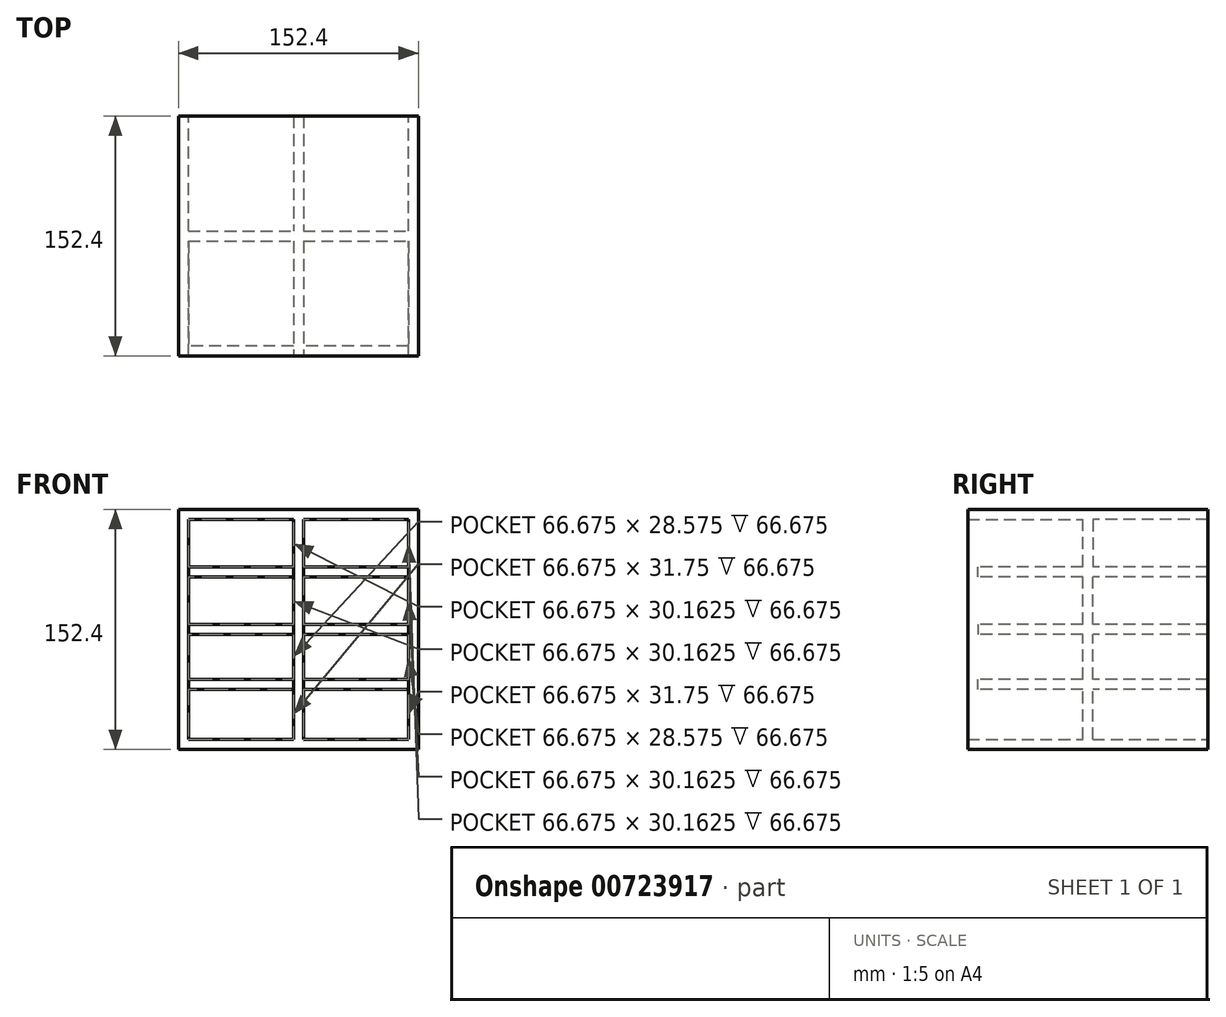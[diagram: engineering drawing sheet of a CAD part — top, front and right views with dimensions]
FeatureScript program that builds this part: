
annotation { "Feature Type Name" : "Feature", "Feature Type Description" : "" }
export const myFeature = defineFeature(function(context is Context, id is Id, definition is map)
    precondition{}
    {
        {
            var Q0;
            Q0=qCreatedBy(makeId("Front.planeOp"),FACE);
            var sketch = newSketch(context, id + "F0", { "sketchPlane" : qUnion([Q0])});
            skLineSegment(sketch, "E0.bottom", {"start": v(76.2, 76.2) * mm, "end": v(-76.2, 76.2) * mm});
            skLineSegment(sketch, "E0.top", {"start": v(76.2, -76.2) * mm, "end": v(-76.2, -76.2) * mm});
            skLineSegment(sketch, "E0.left", {"start": v(76.2, 76.2) * mm, "end": v(76.2, -76.2) * mm});
            skLineSegment(sketch, "E0.right", {"start": v(-76.2, 76.2) * mm, "end": v(-76.2, -76.2) * mm});
            skPoint(sketch, "E0.middle", {"position": v(0, 0) * mm});
            skSolve(sketch);
        }
        {
            var Q0;
            Q0 = qSketchRegion(id + "F0", true);
            extrude(context, id + "F1", {"entities" : qUnion([Q0]), "depth" : 152.4 * mm, "offsetDistance" : 25.4 * mm, "symmetric" : true});
        }
        {
            var Q0;
            Q0=makeQuery(id+"F1.opExtrude","CAP_FACE",FACE,{"disambiguationData":[OSD([sQuery(id+"F0.wireOp",EDGE,"E0.bottom"),sQuery(id+"F0.wireOp",EDGE,"E0.top"),sQuery(id+"F0.wireOp",EDGE,"E0.left"),sQuery(id+"F0.wireOp",EDGE,"E0.right")])],"isStart":false});
            shell(context, id + "F2", {"entities" : qUnion([Q0]), "thickness" : 6.35 * mm});
        }
        {
            var Q0;
            Q0=makeQuery(id+"F1.opExtrude","CAP_FACE",FACE,{"disambiguationData":[OSD([sQuery(id+"F0.wireOp",EDGE,"E0.bottom"),sQuery(id+"F0.wireOp",EDGE,"E0.top"),sQuery(id+"F0.wireOp",EDGE,"E0.left"),sQuery(id+"F0.wireOp",EDGE,"E0.right")])],"isStart":false});
            var sketch = newSketch(context, id + "F3", { "sketchPlane" : qUnion([Q0])});
            skLineSegment(sketch, "E1.bottom", {"start": v(-3.18, 69.85) * mm, "end": v(3.18, 69.85) * mm});
            skLineSegment(sketch, "E1.top", {"start": v(-3.18, -69.85) * mm, "end": v(3.18, -69.85) * mm});
            skLineSegment(sketch, "E1.left", {"start": v(-3.18, 69.85) * mm, "end": v(-3.18, -69.85) * mm});
            skLineSegment(sketch, "E1.right", {"start": v(3.18, 69.85) * mm, "end": v(3.18, -69.85) * mm});
            skPoint(sketch, "E1.middle", {"position": v(0, 0) * mm});
            skSolve(sketch);
        }
        {
            var Q0;
            Q0 = qSketchRegion(id + "F3", true);
            extrude(context, id + "F4", {"entities" : qUnion([Q0]), "operationType" : NewBodyOperationType.ADD, "oppositeDirection" : true, "depth" : 152.4 * mm, "offsetDistance" : 25.4 * mm});
        }
        {
            var Q0;
            Q0=makeQuery(id+"F2.opShell","OFFSET_FACE",FACE,{"disambiguationData":[OSD([sQuery(id+"F0.wireOp",EDGE,"E0.right")])]});
            var sketch = newSketch(context, id + "F5", { "sketchPlane" : qUnion([Q0])});
            skLineSegment(sketch, "E2.bottom", {"start": v(69.85, 3.18) * mm, "end": v(-69.85, 3.18) * mm});
            skLineSegment(sketch, "E2.top", {"start": v(69.85, -3.18) * mm, "end": v(-69.85, -3.18) * mm});
            skLineSegment(sketch, "E2.left", {"start": v(69.85, 3.18) * mm, "end": v(69.85, -3.18) * mm});
            skLineSegment(sketch, "E2.right", {"start": v(-69.85, 3.18) * mm, "end": v(-69.85, -3.18) * mm});
            skPoint(sketch, "E2.middle", {"position": v(0, 0) * mm});
            skLineSegment(sketch, "E3", {"start": v(-69.85, 3.18) * mm, "end": v(-69.85, 36.51) * mm});
            skLineSegment(sketch, "E4", {"start": v(69.85, 3.18) * mm, "end": v(69.85, 36.51) * mm});
            skLineSegment(sketch, "E5.bottom", {"start": v(69.85, 33.34) * mm, "end": v(-69.85, 33.34) * mm});
            skLineSegment(sketch, "E5.top", {"start": v(69.85, 39.69) * mm, "end": v(-69.85, 39.69) * mm});
            skLineSegment(sketch, "E5.left", {"start": v(69.85, 33.34) * mm, "end": v(69.85, 39.69) * mm});
            skLineSegment(sketch, "E5.right", {"start": v(-69.85, 33.34) * mm, "end": v(-69.85, 39.69) * mm});
            skPoint(sketch, "E5.middle", {"position": v(0, 36.51) * mm});
            skLineSegment(sketch, "E6.bottom", {"start": v(69.85, -38.1) * mm, "end": v(-69.85, -38.1) * mm});
            skLineSegment(sketch, "E6.top", {"start": v(69.85, -31.75) * mm, "end": v(-69.85, -31.75) * mm});
            skLineSegment(sketch, "E6.left", {"start": v(69.85, -38.1) * mm, "end": v(69.85, -31.75) * mm});
            skLineSegment(sketch, "E6.right", {"start": v(-69.85, -38.1) * mm, "end": v(-69.85, -31.75) * mm});
            skPoint(sketch, "E6.middle", {"position": v(0, -34.92) * mm});
            skSolve(sketch);
        }
        {
            var Q0;
            Q0=makeQuery(id+"F5.imprint","IMPRINT",FACE,{"disambiguationData":[TD([[makeQuery(id+"F5.imprint","IMPRINT",EDGE,{"derivedFrom":sQuery(id+"F5.wireOp",EDGE,"E2.bottom")}),1.0]])]});
            var Q1;
            {var subQ1=sQuery(id+"F5.wireOp",EDGE,"E5.bottom");Q1=makeQuery(id+"F5.imprint","IMPRINT",FACE,{"disambiguationData":[TD([[makeQuery(id+"F5.imprint","IMPRINT",EDGE,{"derivedFrom":subQ1}),-1.0]])]});}
            var Q2;
            Q2=makeQuery(id+"F5.imprint","IMPRINT",FACE,{"disambiguationData":[TD([[makeQuery(id+"F5.imprint","IMPRINT",EDGE,{"derivedFrom":sQuery(id+"F5.wireOp",EDGE,"E6.bottom")}),-1.0]])]});
            extrude(context, id + "F6", {"entities" : qUnion([Q0, Q1, Q2]), "operationType" : NewBodyOperationType.ADD, "depth" : 139.7 * mm, "offsetDistance" : 25.4 * mm});
        }
        {
            var Q0;
            {var subQ0=sQuery(id+"F0.wireOp",EDGE,"E0.bottom");var subQ1=sQuery(id+"F0.wireOp",EDGE,"E0.top");var subQ2=sQuery(id+"F0.wireOp",EDGE,"E0.right");Q0=makeQuery(id+"F4.boolean.opBoolean","SPLIT",FACE,{"disambiguationData":[TD([makeQuery(id+"F2.opShell","OFFSET_FACE",FACE,{"disambiguationData":[OSD([subQ2])]})])],"derivedFrom":makeQuery(id+"F2.opShell","OFFSET_FACE",FACE,{"disambiguationData":[OSD([subQ0,subQ1,sQuery(id+"F0.wireOp",EDGE,"E0.left"),subQ2])]})});}
            var Q1;
            {var subQ0=sQuery(id+"F0.wireOp",EDGE,"E0.bottom");var subQ1=sQuery(id+"F0.wireOp",EDGE,"E0.top");var subQ2=sQuery(id+"F0.wireOp",EDGE,"E0.left");Q1=makeQuery(id+"F4.boolean.opBoolean","SPLIT",FACE,{"disambiguationData":[TD([makeQuery(id+"F2.opShell","OFFSET_FACE",FACE,{"disambiguationData":[OSD([subQ2])]})])],"derivedFrom":makeQuery(id+"F2.opShell","OFFSET_FACE",FACE,{"disambiguationData":[OSD([subQ0,subQ1,subQ2,sQuery(id+"F0.wireOp",EDGE,"E0.right")])]})});}
            extrude(context, id + "F7", {"entities" : qUnion([Q0, Q1]), "operationType" : NewBodyOperationType.REMOVE, "oppositeDirection" : true, "depth" : 127 * mm, "offsetDistance" : 25.4 * mm, "symmetric" : true});
        }
        {
            var Q0;
            Q0=makeQuery(id+"F1.opExtrude","SWEPT_FACE",FACE,{"disambiguationData":[OSD([sQuery(id+"F0.wireOp",EDGE,"E0.bottom")])]});
            var sketch = newSketch(context, id + "F8", { "sketchPlane" : qUnion([Q0])});
            skLineSegment(sketch, "E7.bottom", {"start": v(76.2, -3.18) * mm, "end": v(-76.2, -3.18) * mm});
            skLineSegment(sketch, "E7.top", {"start": v(76.2, 3.18) * mm, "end": v(-76.2, 3.18) * mm});
            skLineSegment(sketch, "E7.left", {"start": v(76.2, -3.18) * mm, "end": v(76.2, 3.18) * mm});
            skLineSegment(sketch, "E7.right", {"start": v(-76.2, -3.18) * mm, "end": v(-76.2, 3.18) * mm});
            skPoint(sketch, "E7.middle", {"position": v(0, 0) * mm});
            skSolve(sketch);
        }
        {
            var Q0;
            Q0 = qSketchRegion(id + "F8", true);
            extrude(context, id + "F9", {"entities" : qUnion([Q0]), "operationType" : NewBodyOperationType.ADD, "oppositeDirection" : true, "depth" : 152.4 * mm, "offsetDistance" : 25.4 * mm});
        }
    });
